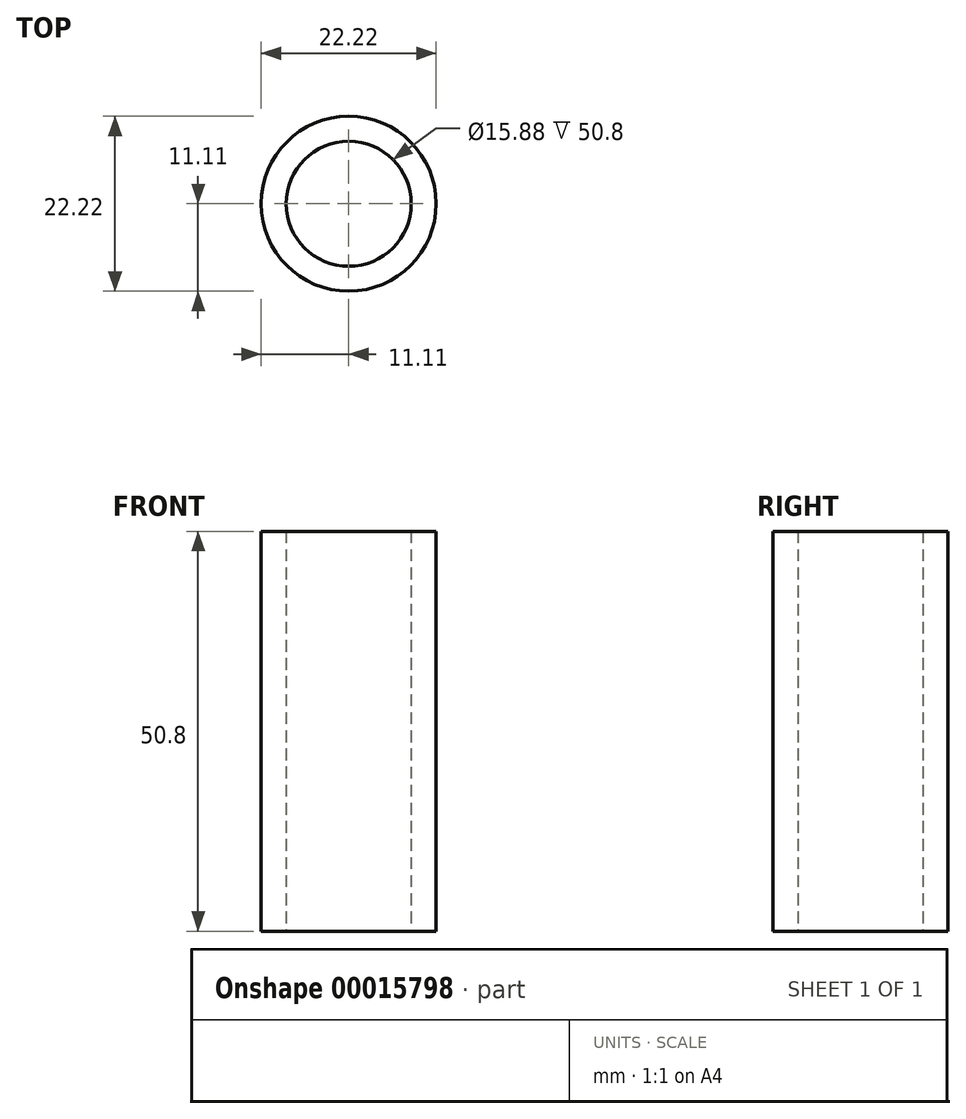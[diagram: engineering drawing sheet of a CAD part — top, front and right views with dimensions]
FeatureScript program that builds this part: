
annotation { "Feature Type Name" : "Feature", "Feature Type Description" : "" }
export const myFeature = defineFeature(function(context is Context, id is Id, definition is map)
    precondition{}
    {
        {
            var Q0;
            Q0=qCreatedBy(makeId("Top.planeOp"),FACE);
            var sketch = newSketch(context, id + "F0", { "sketchPlane" : qUnion([Q0])});
            skCircle(sketch, "E0", {"center": v(0, 0) * mm, "radius": 11.11 * mm});
            skCircle(sketch, "E1", {"center": v(0, 0) * mm, "radius": 7.94 * mm});
            skSolve(sketch);
        }
        {
            var Q0;
            Q0=qSketchRegion(id+"F0",true);
            extrude(context, id + "F1", {"entities" : qUnion([Q0]), "depth" : 50.8 * mm});
        }
    });
